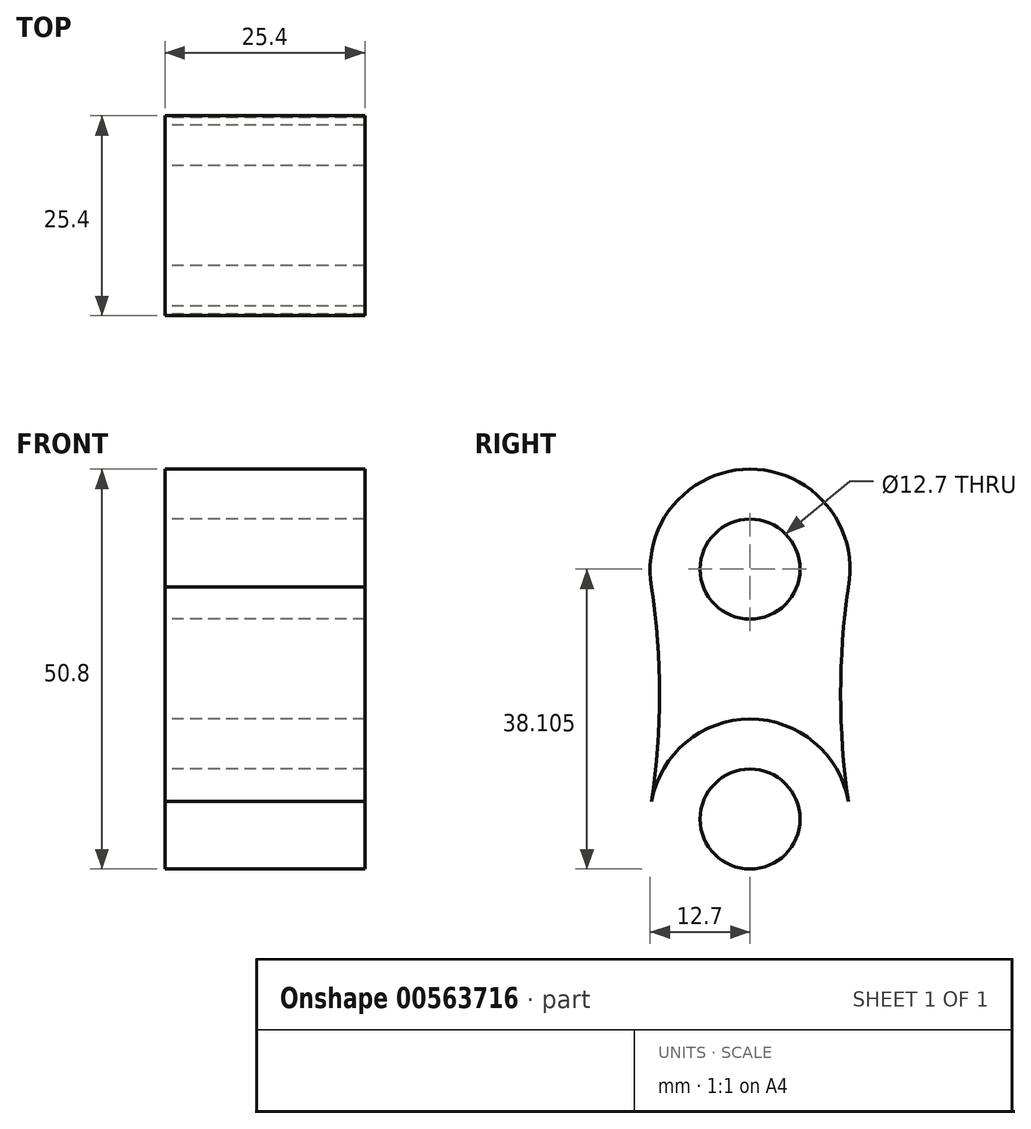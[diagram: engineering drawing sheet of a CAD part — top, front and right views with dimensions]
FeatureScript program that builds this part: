
annotation { "Feature Type Name" : "Feature", "Feature Type Description" : "" }
export const myFeature = defineFeature(function(context is Context, id is Id, definition is map)
    precondition{}
    {
        {
            var Q0;
            Q0=qCreatedBy(makeId("Right.planeOp"),FACE);
            var sketch = newSketch(context, id + "F0", { "sketchPlane" : qUnion([Q0])});
            skCircle(sketch, "E0", {"center": v(0, 15.88) * mm, "radius": 6.35 * mm});
            skCircle(sketch, "E1", {"center": v(0, 15.88) * mm, "radius": 12.7 * mm});
            skCircle(sketch, "E2.MirrorC", {"center": v(0, -15.88) * mm, "radius": 6.35 * mm});
            skCircle(sketch, "E3.MirrorC", {"center": v(0, -15.88) * mm, "radius": 12.7 * mm});
            skArc(sketch, "E4", {"start": v(-21.5, 30.3) * mm, "mid": v(-41.75, 21.16) * mm, "end": v(-59.28, 7.5) * mm});
            skArc(sketch, "E5", {"start": v(-12.5, -13.6) * mm, "mid": v(-11.5, 0) * mm, "end": v(-12.5, 13.6) * mm});
            skArc(sketch, "E6", {"start": v(12.5, 13.6) * mm, "mid": v(11.5, 0) * mm, "end": v(12.5, -13.6) * mm});
            skSolve(sketch);
        }
        {
            var Q0;
            {var subQ2=sQuery(id+"F0.wireOp",EDGE,"e35c3605-ffbe-408e-a598-43df0ac5c0f6");Q0=makeQuery(id+"F0.imprint","IMPRINT",FACE,{"disambiguationData":[TD([[makeQuery(id+"F0.imprint","IMPRINT",EDGE,{"derivedFrom":subQ2}),-1.0]])]});}
            var Q1;
            Q1=makeQuery(id+"F0.imprint","IMPRINT",FACE,{"disambiguationData":[TD([[makeQuery(id+"F0.imprint","IMPRINT",EDGE,{"derivedFrom":sQuery(id+"F0.wireOp",EDGE,"E0")}),-1.0]])]});
            var Q2;
            Q2=makeQuery(id+"F0.imprint","IMPRINT",FACE,{"disambiguationData":[TD([[makeQuery(id+"F0.imprint","IMPRINT",EDGE,{"derivedFrom":sQuery(id+"F0.wireOp",EDGE,"E2.MirrorC")}),1.0]])]});
            var Q3;
            {var subQ0=sQuery(id+"F0.wireOp",EDGE,"e074c89a-0b23-45a3-a14e-9c47273ea14d");Q3=makeQuery(id+"F0.imprint","IMPRINT",FACE,{"disambiguationData":[TD([[makeQuery(id+"F0.imprint","IMPRINT",EDGE,{"derivedFrom":subQ0}),1.0]])]});}
            var Q4;
            {var subQ0=sQuery(id+"F0.wireOp",EDGE,"317ac0b0-b18f-42e3-a7ce-9aac6ec015a70.MirrorCS");Q4=makeQuery(id+"F0.imprint","IMPRINT",FACE,{"disambiguationData":[TD([[makeQuery(id+"F0.imprint","IMPRINT",EDGE,{"derivedFrom":subQ0}),-1.0]])]});}
            var Q5;
            {var subQ0=sQuery(id+"F0.wireOp",EDGE,"E5");Q5=makeQuery(id+"F0.imprint","IMPRINT",FACE,{"disambiguationData":[TD([[makeQuery(id+"F0.imprint","IMPRINT",EDGE,{"derivedFrom":subQ0}),-1.0]])]});}
            extrude(context, id + "F1", {"entities" : qUnion([Q0, Q1, Q2, Q3, Q4, Q5]), "depth" : 25.4 * mm});
        }
    });
